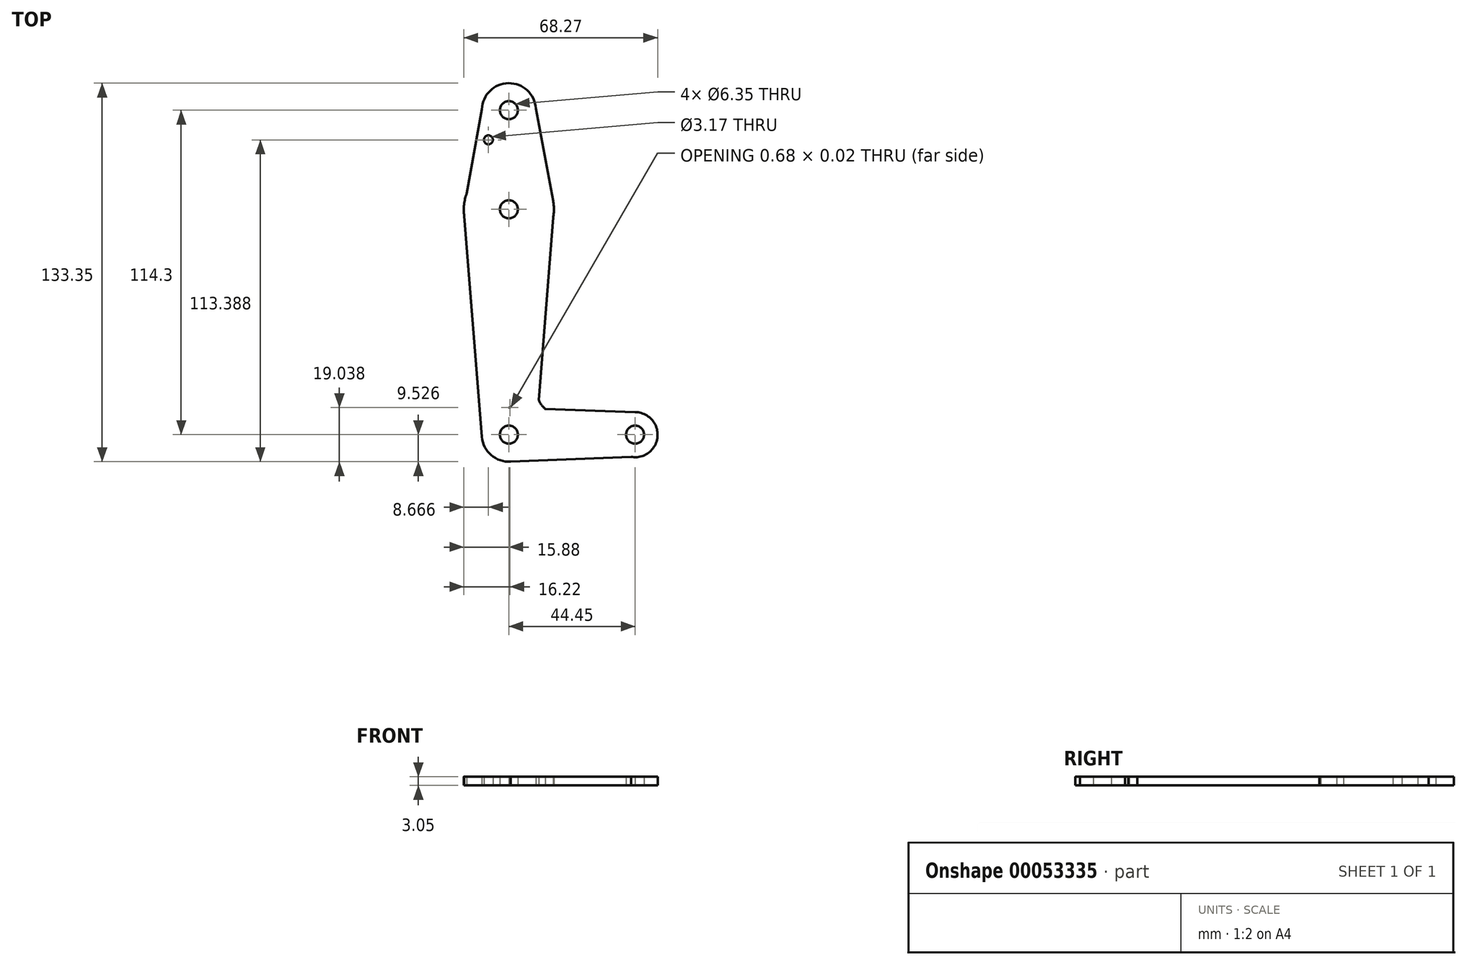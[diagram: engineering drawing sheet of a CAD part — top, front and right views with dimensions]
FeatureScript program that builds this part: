
annotation { "Feature Type Name" : "Feature", "Feature Type Description" : "" }
export const myFeature = defineFeature(function(context is Context, id is Id, definition is map)
    precondition{}
    {
        {
            var Q0;
            Q0=qCreatedBy(makeId("Top.planeOp"),FACE);
            var sketch = newSketch(context, id + "F0", { "sketchPlane" : qUnion([Q0])});
            skLineSegment(sketch, "E0", {"start": v(-44.45, -323.96) * mm, "end": v(-44.45, -327.14) * mm});
            skLineSegment(sketch, "E1", {"start": v(-49.84, -331.82) * mm, "end": v(-49.84, -331.82) * mm});
            skArc(sketch, "E2", {"start": v(-60.14, -361.3) * mm, "mid": v(-54.79, -370.94) * mm, "end": v(-44.45, -374.76) * mm});
            skCircle(sketch, "E3", {"center": v(-44.45, -438.26) * mm, "radius": 9.53 * mm});
            skLineSegment(sketch, "E4.trimOffspring", {"start": v(-44.45, -435.09) * mm, "end": v(-44.45, -438.26) * mm});
            skLineSegment(sketch, "E5", {"start": v(-44.45, -428.01) * mm, "end": v(-44.45, -428.74) * mm});
            skCircle(sketch, "E6", {"center": v(0, -438.26) * mm, "radius": 7.94 * mm});
            skLineSegment(sketch, "E7", {"start": v(-53.5, -320.97) * mm, "end": v(-53.97, -323.63) * mm});
            skLineSegment(sketch, "E8", {"start": v(-60.32, -358.99) * mm, "end": v(-60.14, -361.3) * mm});
            skLineSegment(sketch, "E9", {"start": v(-44.45, -428.74) * mm, "end": v(-43.77, -428.76) * mm});
            skLineSegment(sketch, "E10", {"start": v(-44.38, -447.79) * mm, "end": v(-43.84, -447.77) * mm});
            skCircle(sketch, "E11", {"center": v(-44.45, -323.96) * mm, "radius": 3.18 * mm});
            skCircle(sketch, "E12", {"center": v(-44.45, -358.89) * mm, "radius": 3.18 * mm});
            skCircle(sketch, "E13", {"center": v(-44.45, -438.26) * mm, "radius": 3.18 * mm});
            skCircle(sketch, "E14", {"center": v(0, -438.26) * mm, "radius": 3.18 * mm});
            skLineSegment(sketch, "E15", {"start": v(2.07, -445.93) * mm, "end": v(-1.52, -446.05) * mm});
            skLineSegment(sketch, "E16", {"start": v(-44.45, -438.26) * mm, "end": v(-44.45, -441.44) * mm});
            skPoint(sketch, "E17.orphan", {"position": v(-44.38, -581.48) * mm});
            skLineSegment(sketch, "E18", {"start": v(-44.45, -438.26) * mm, "end": v(-41.28, -438.26) * mm});
            skPoint(sketch, "E19.end.orphan", {"position": v(-28.84, -356) * mm});
            skPoint(sketch, "E20.orphan", {"position": v(-28.84, -361.79) * mm});
            skArc(sketch, "E21.trimOffspring", {"start": v(-28.84, -356) * mm, "mid": v(-45.96, -343.09) * mm, "end": v(-60.32, -358.99) * mm});
            skCircle(sketch, "E22", {"center": v(-44.45, -358.89) * mm, "radius": 15.88 * mm});
            skLineSegment(sketch, "E23.trimOffspring", {"start": v(-42.13, -447.5) * mm, "end": v(-46.1, -447.64) * mm});
            skPoint(sketch, "E24.orphan", {"position": v(0, -430.33) * mm});
            skPoint(sketch, "E25.orphan", {"position": v(0, -446.2) * mm});
            skArc(sketch, "E26.trimOffspring", {"start": v(-46.87, -333.18) * mm, "mid": v(-45.67, -333.41) * mm, "end": v(-44.45, -333.49) * mm});
            skLineSegment(sketch, "E27", {"start": v(-59.3, -353.27) * mm, "end": v(-60.32, -358.99) * mm});
            skPoint(sketch, "E28.startSnap0", {"position": v(-36.8, -318.28) * mm});
            skPoint(sketch, "E28.start.orphan", {"position": v(-36.8, -329.65) * mm});
            skArc(sketch, "E29.trimOffspring", {"start": v(-53.5, -320.97) * mm, "mid": v(-53.82, -322.28) * mm, "end": v(-53.97, -323.63) * mm});
            skCircle(sketch, "E30", {"center": v(-44.45, -323.96) * mm, "radius": 9.53 * mm});
            skLineSegment(sketch, "E31", {"start": v(-53.97, -323.63) * mm, "end": v(-59.3, -353.27) * mm});
            skLineSegment(sketch, "E32", {"start": v(-34.94, -323.35) * mm, "end": v(-28.84, -356) * mm});
            skLineSegment(sketch, "E33", {"start": v(-60.14, -361.3) * mm, "end": v(-53.94, -439.02) * mm});
            skLineSegment(sketch, "E34", {"start": v(-28.84, -361.79) * mm, "end": v(-34.17, -429.1) * mm});
            skLineSegment(sketch, "E35", {"start": v(-34.17, -429.1) * mm, "end": v(0, -430.33) * mm});
            skLineSegment(sketch, "E36", {"start": v(-43.84, -447.77) * mm, "end": v(2.07, -445.93) * mm});
            skArc(sketch, "E37", {"start": v(-33.37, -419.05) * mm, "mid": v(-31.9, -428.96) * mm, "end": v(-21.89, -429.55) * mm});
            skCircle(sketch, "E38", {"center": v(-51.66, -334.4) * mm, "radius": 1.59 * mm});
            skLineSegment(sketch, "E39.trimOffspring", {"start": v(-7.94, -438.26) * mm, "end": v(0, -438.26) * mm});
            skLineSegment(sketch, "E40.trimOffspring", {"start": v(-44.45, -447.58) * mm, "end": v(-44.45, -447.79) * mm});
            skArc(sketch, "E41.trimOffspring", {"start": v(-34.04, -427.49) * mm, "mid": v(-33.63, -427.45) * mm, "end": v(-33.21, -427.4) * mm});
            skLineSegment(sketch, "E42.trimOffspring", {"start": v(-44.45, -355.71) * mm, "end": v(-44.45, -362.06) * mm});
            skSolve(sketch);
        }
        {
            var Q0;
            Q0 = qSketchRegion(id + "F0", true);
            extrude(context, id + "F1", {"entities" : qUnion([Q0]), "depth" : 3.05 * mm});
        }
        {
            var Q0;
            Q0 = qSketchRegion(id + "F0", true);
            extrude(context, id + "F2", {"entities" : qUnion([Q0]), "operationType" : NewBodyOperationType.ADD, "depth" : 3.05 * mm});
        }
        {
            var Q0;
            Q0 = qSketchRegion(id + "F0", true);
            extrude(context, id + "F3", {"entities" : qUnion([Q0]), "operationType" : NewBodyOperationType.ADD, "depth" : 3.05 * mm});
        }
        {
            var Q0;
            Q0 = qSketchRegion(id + "F0", true);
            extrude(context, id + "F4", {"entities" : qUnion([Q0]), "operationType" : NewBodyOperationType.ADD, "depth" : 3.05 * mm});
        }
        {
            var Q0;
            Q0 = qSketchRegion(id + "F0", true);
            extrude(context, id + "F5", {"entities" : qUnion([Q0]), "operationType" : NewBodyOperationType.ADD, "depth" : 3.05 * mm});
        }
    });
